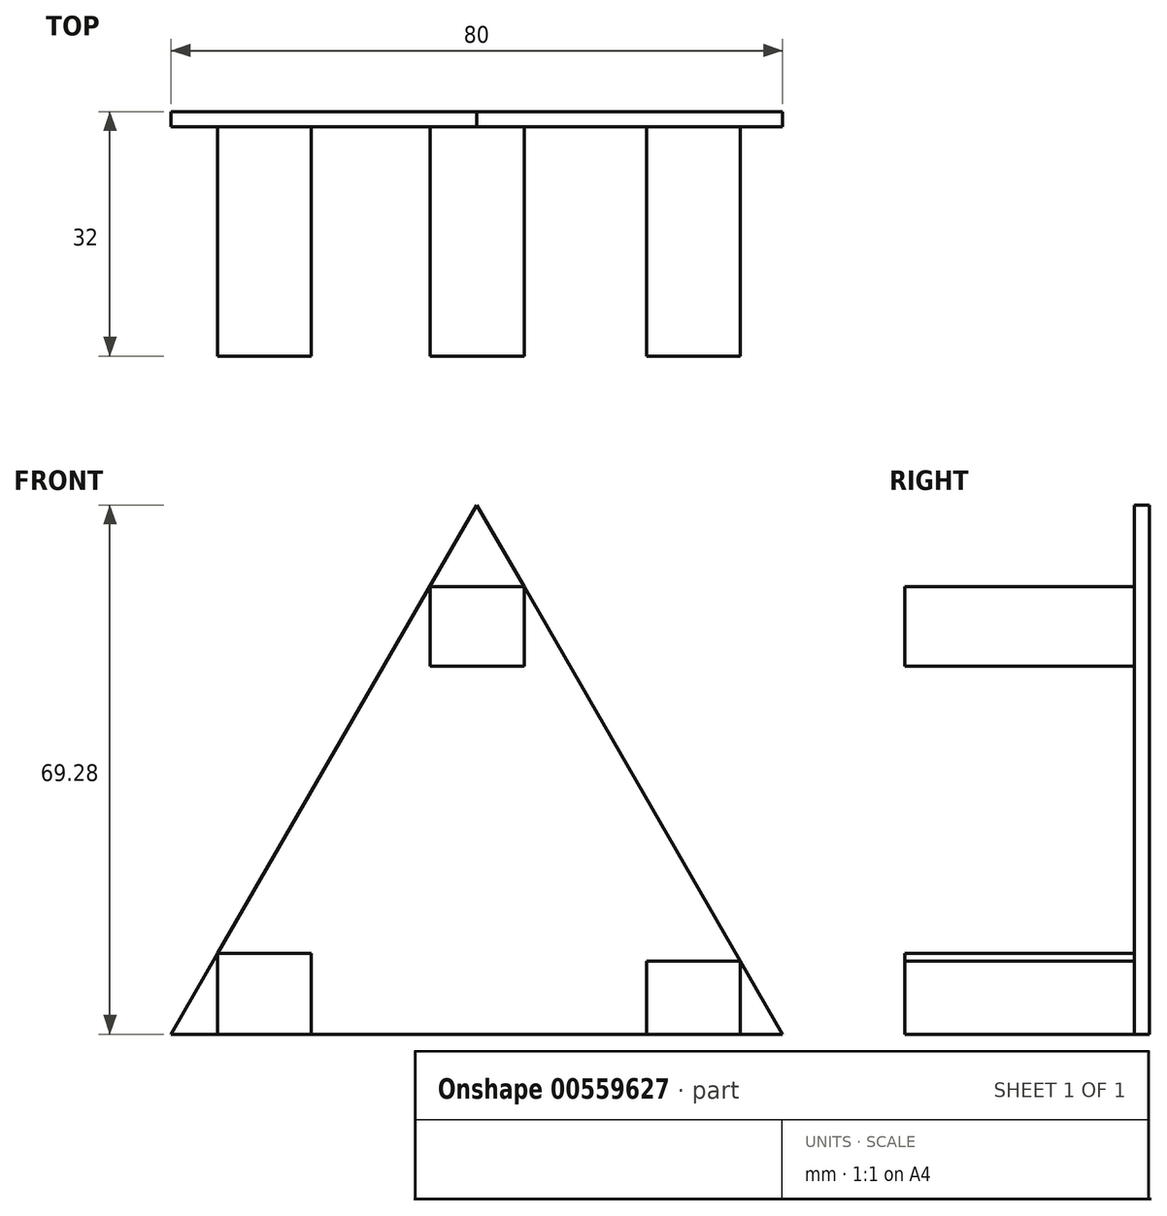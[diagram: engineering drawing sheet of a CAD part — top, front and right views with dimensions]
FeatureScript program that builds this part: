
annotation { "Feature Type Name" : "Feature", "Feature Type Description" : "" }
export const myFeature = defineFeature(function(context is Context, id is Id, definition is map)
    precondition{}
    {
        {
            var Q0;
            Q0=qCreatedBy(makeId("Front.planeOp"),FACE);
            var sketch = newSketch(context, id + "F0", { "sketchPlane" : qUnion([Q0])});
            skLineSegment(sketch, "E0", {"start": v(0, 0) * mm, "end": v(-40, -69.28) * mm});
            skLineSegment(sketch, "E1", {"start": v(-40, -69.28) * mm, "end": v(40, -69.28) * mm});
            skLineSegment(sketch, "E2", {"start": v(40, -69.28) * mm, "end": v(0, 0) * mm});
            skSolve(sketch);
        }
        {
            var Q0;
            Q0 = qSketchRegion(id + "F0", true);
            extrude(context, id + "F1", {"entities" : qUnion([Q0]), "oppositeDirection" : true, "depth" : 2 * mm, "offsetDistance" : 25 * mm});
        }
        {
            var Q0;
            Q0=makeQuery(id+"F1.opExtrude","CAP_FACE",FACE,{"disambiguationData":[OSD([sQuery(id+"F0.wireOp",EDGE,"E0"),sQuery(id+"F0.wireOp",EDGE,"E1"),sQuery(id+"F0.wireOp",EDGE,"E2")])],"isStart":true});
            var sketch = newSketch(context, id + "F2", { "sketchPlane" : qUnion([Q0])});
            skLineSegment(sketch, "E3.bottom", {"start": v(-6.1, -21.1) * mm, "end": v(6.17, -21.1) * mm});
            skLineSegment(sketch, "E3.top", {"start": v(-6.1, -10.7) * mm, "end": v(6.17, -10.7) * mm});
            skLineSegment(sketch, "E3.left", {"start": v(-6.1, -21.1) * mm, "end": v(-6.1, -10.7) * mm});
            skLineSegment(sketch, "E3.right", {"start": v(6.17, -21.1) * mm, "end": v(6.17, -10.7) * mm});
            skLineSegment(sketch, "E4.bottom", {"start": v(-33.9, -58.7) * mm, "end": v(-21.67, -58.7) * mm});
            skLineSegment(sketch, "E4.top", {"start": v(-33.9, -69.28) * mm, "end": v(-21.67, -69.28) * mm});
            skLineSegment(sketch, "E4.left", {"start": v(-33.9, -58.7) * mm, "end": v(-33.9, -69.28) * mm});
            skLineSegment(sketch, "E4.right", {"start": v(-21.67, -58.7) * mm, "end": v(-21.67, -69.28) * mm});
            skLineSegment(sketch, "E5.bottom", {"start": v(22.24, -69.28) * mm, "end": v(34.48, -69.28) * mm});
            skLineSegment(sketch, "E5.top", {"start": v(22.24, -59.71) * mm, "end": v(34.48, -59.71) * mm});
            skLineSegment(sketch, "E5.left", {"start": v(22.24, -69.28) * mm, "end": v(22.24, -59.71) * mm});
            skLineSegment(sketch, "E5.right", {"start": v(34.48, -69.28) * mm, "end": v(34.48, -59.71) * mm});
            skSolve(sketch);
        }
        {
            var Q0;
            Q0 = qSketchRegion(id + "F2", true);
            extrude(context, id + "F3", {"entities" : qUnion([Q0]), "operationType" : NewBodyOperationType.ADD, "depth" : 30 * mm, "offsetDistance" : 25 * mm});
        }
    });
